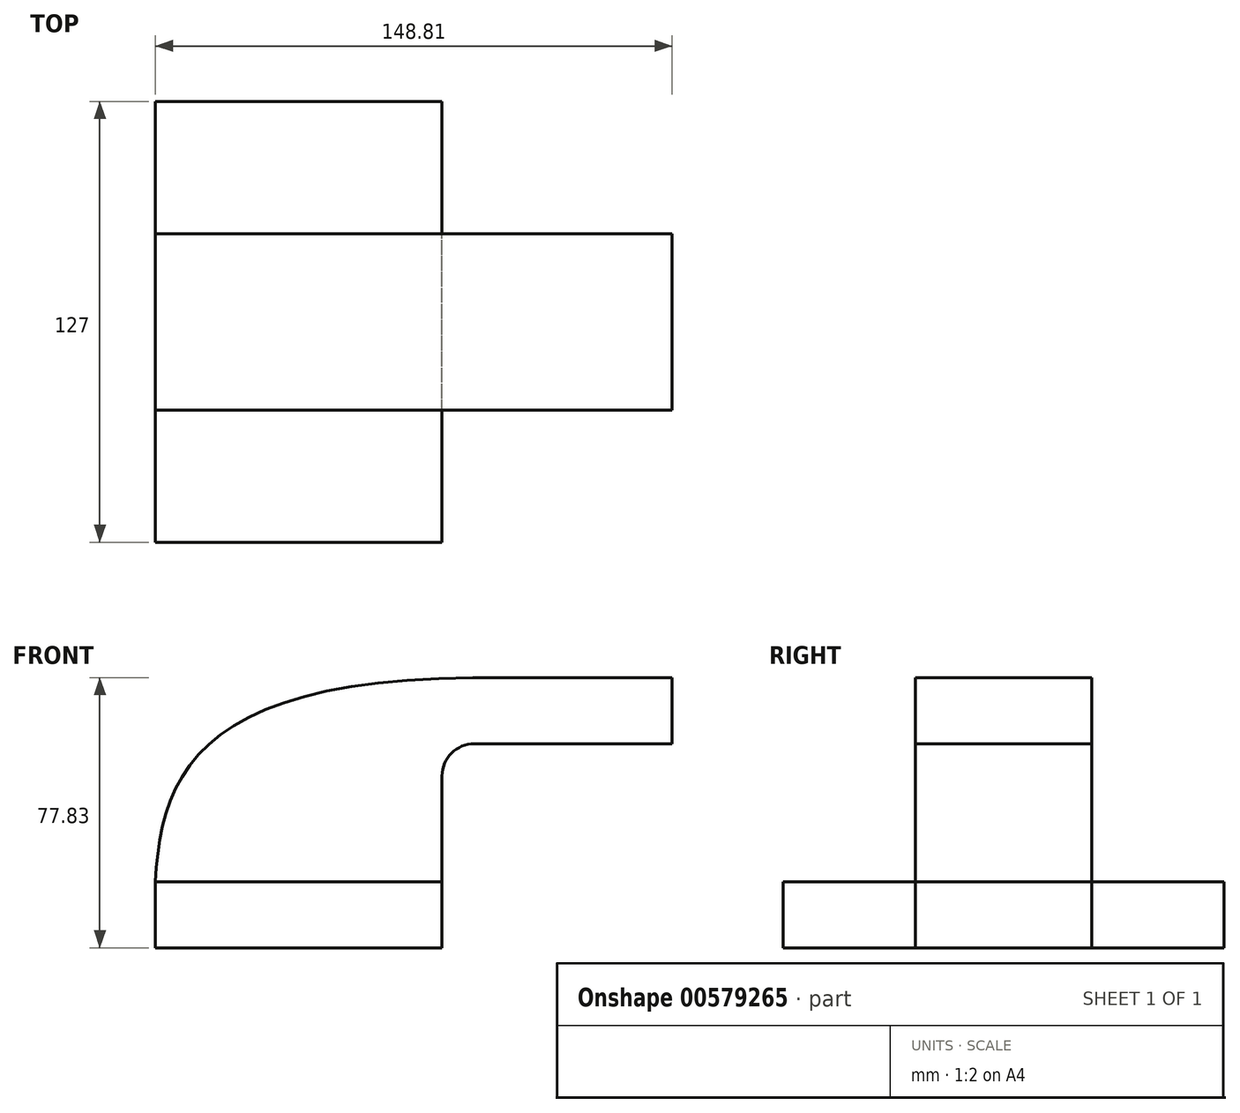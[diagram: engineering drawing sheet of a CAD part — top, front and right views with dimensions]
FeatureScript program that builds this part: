
annotation { "Feature Type Name" : "Feature", "Feature Type Description" : "" }
export const myFeature = defineFeature(function(context is Context, id is Id, definition is map)
    precondition{}
    {
        {
            var Q0;
            Q0=qCreatedBy(makeId("Front.planeOp"),FACE);
            var sketch = newSketch(context, id + "F0", { "sketchPlane" : qUnion([Q0])});
            skLineSegment(sketch, "E0.bottom", {"start": v(-41.28, -9.53) * mm, "end": v(41.28, -9.53) * mm});
            skLineSegment(sketch, "E0.top", {"start": v(-41.28, 9.52) * mm, "end": v(41.28, 9.52) * mm});
            skLineSegment(sketch, "E0.left", {"start": v(-41.27, -9.53) * mm, "end": v(-41.28, 9.52) * mm});
            skLineSegment(sketch, "E0.right", {"start": v(41.28, -9.53) * mm, "end": v(41.28, 9.52) * mm});
            skPoint(sketch, "E0.middle", {"position": v(0, 0) * mm});
            skLineSegment(sketch, "E1.bottom", {"start": v(69.43, 35.97) * mm, "end": v(145.63, 35.97) * mm});
            skLineSegment(sketch, "E1.top", {"start": v(69.43, 99.47) * mm, "end": v(145.63, 99.47) * mm});
            skLineSegment(sketch, "E1.left", {"start": v(69.43, 35.97) * mm, "end": v(69.43, 99.47) * mm});
            skLineSegment(sketch, "E1.right", {"start": v(145.63, 35.97) * mm, "end": v(145.63, 99.47) * mm});
            skPoint(sketch, "E1.middle", {"position": v(107.53, 67.72) * mm});
            skLineSegment(sketch, "E2", {"start": v(41.27, 9.52) * mm, "end": v(41.27, 40) * mm});
            skArc(sketch, "E3", {"start": v(41.27, 40) * mm, "mid": v(43.98, 46.55) * mm, "end": v(50.52, 49.25) * mm});
            skLineSegment(sketch, "E4", {"start": v(50.52, 49.25) * mm, "end": v(107.53, 49.25) * mm});
            skLineSegment(sketch, "E5.0", {"start": v(50.52, 68.3) * mm, "end": v(107.53, 68.3) * mm});
            skArc(sketch, "E5.1", {"start": v(22.22, 40) * mm, "mid": v(30.51, 60.02) * mm, "end": v(50.52, 68.3) * mm});
            skLineSegment(sketch, "E5.2", {"start": v(22.22, 9.52) * mm, "end": v(22.22, 40) * mm});
            skLineSegment(sketch, "E6", {"start": v(107.53, 99.47) * mm, "end": v(107.53, 35.97) * mm});
            skFitSpline(sketch, "E7", {"points": [v(-41.28, 9.53) * mm, v(50.52, 68.3) * mm], "startDerivative": vector(4.27, 94.71) * mm, "endDerivative": vector(234.6, 1.66) * mm});
            skSolve(sketch);
        }
        {
            var Q0;
            Q0=makeQuery(id+"F0.imprint","IMPRINT",FACE,{"disambiguationData":[TD([[makeQuery(id+"F0.imprint","IMPRINT",EDGE,{"derivedFrom":sQuery(id+"F0.wireOp",EDGE,"E0.bottom")}),1.0]])]});
            extrude(context, id + "F1", {"entities" : qUnion([Q0]), "endBound" : BoundingType.SYMMETRIC, "depth" : 127 * mm, "offsetDistance" : 25.4 * mm});
        }
        {
            var Q0;
            {var subQ0=sQuery(id+"F0.wireOp",EDGE,"E7");var subQ1=sQuery(id+"F0.wireOp",EDGE,"E5.1");var subQ3=makeQuery(id+"F0.imprint","INTERSECT",VERTEX,{"derivedFrom":[subQ1,subQ0]});Q0=makeQuery(id+"F0.imprint","IMPRINT",FACE,{"disambiguationData":[TD([[makeQuery(id+"F0.imprint","IMPRINT",EDGE,{"disambiguationData":[TD([[subQ3,-1.0]])],"derivedFrom":subQ1}),-1.0]])]});}
            var Q1;
            Q1=makeQuery(id+"F0.imprint","IMPRINT",FACE,{"disambiguationData":[TD([[makeQuery(id+"F0.imprint","IMPRINT",EDGE,{"derivedFrom":sQuery(id+"F0.wireOp",EDGE,"E0.bottom")}),1.0]])]});
            var Q2;
            {var subQ1=sQuery(id+"F0.wireOp",EDGE,"E2");Q2=makeQuery(id+"F0.imprint","IMPRINT",FACE,{"disambiguationData":[TD([[makeQuery(id+"F0.imprint","IMPRINT",EDGE,{"derivedFrom":subQ1}),1.0]])]});}
            var Q3;
            {var subQ0=sQuery(id+"F0.wireOp",EDGE,"E4");var subQ1=sQuery(id+"F0.wireOp",EDGE,"E1.left");var subQ2=makeQuery(id+"F0.imprint","INTERSECT",VERTEX,{"derivedFrom":[subQ1,subQ0]});Q3=makeQuery(id+"F0.imprint","IMPRINT",FACE,{"disambiguationData":[TD([[makeQuery(id+"F0.imprint","IMPRINT",EDGE,{"disambiguationData":[TD([[subQ2,-1.0]])],"derivedFrom":subQ1}),-1.0]])]});}
            extrude(context, id + "F2", {"entities" : qUnion([Q0, Q1, Q2, Q3]), "endBound" : BoundingType.SYMMETRIC, "depth" : 50.8 * mm, "offsetDistance" : 25.4 * mm});
        }
    });
